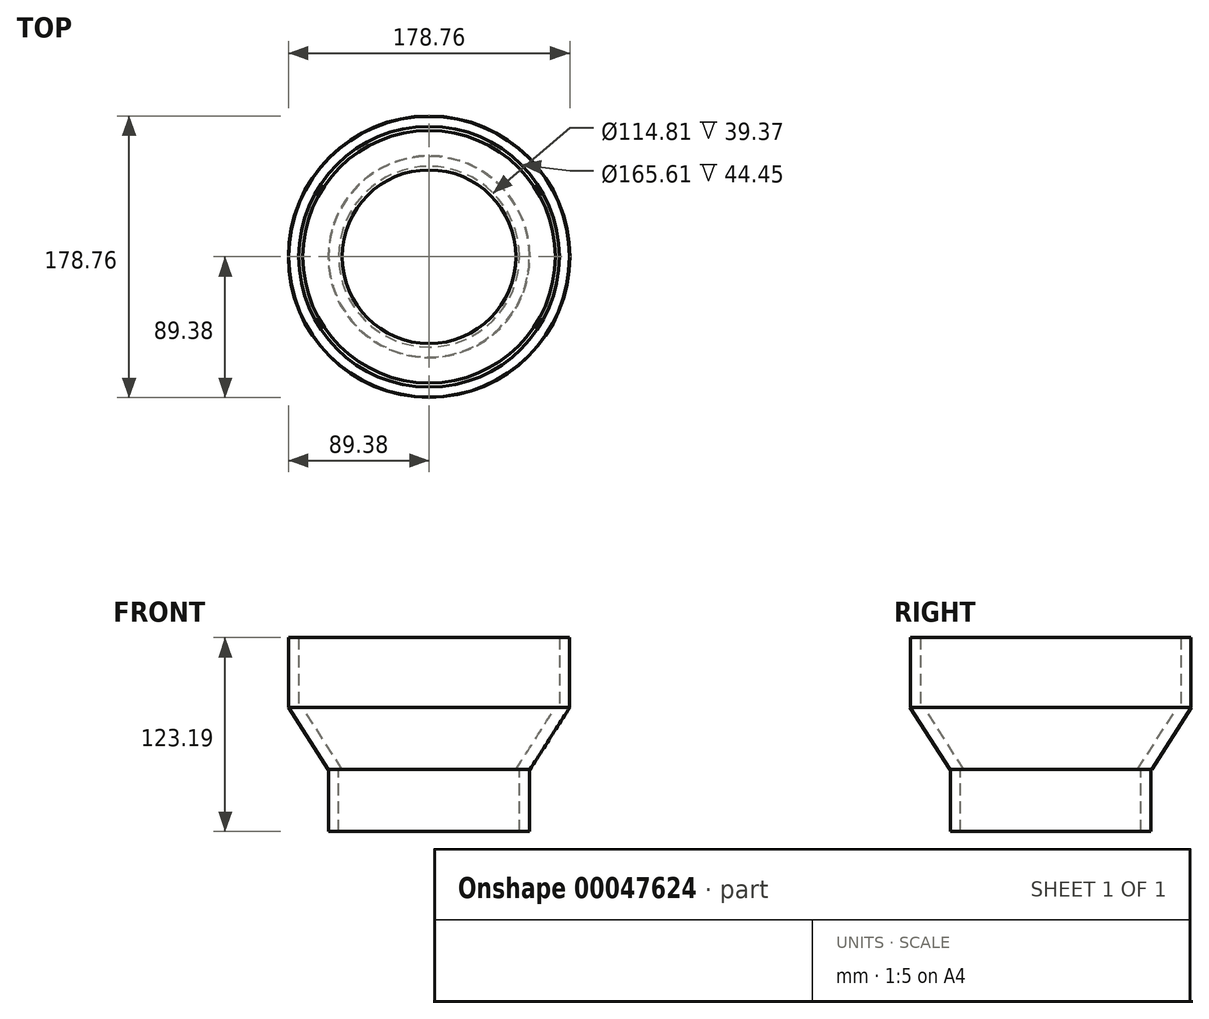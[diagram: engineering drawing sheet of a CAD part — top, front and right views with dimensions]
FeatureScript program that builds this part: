
annotation { "Feature Type Name" : "Feature", "Feature Type Description" : "" }
export const myFeature = defineFeature(function(context is Context, id is Id, definition is map)
    precondition{}
    {
        {
            var Q0;
            Q0=qCreatedBy(makeId("Top.planeOp"),FACE);
            var sketch = newSketch(context, id + "F0", { "sketchPlane" : qUnion([Q0])});
            skCircle(sketch, "E0", {"center": v(0, 0) * mm, "radius": 57.4 * mm});
            skSolve(sketch);
        }
        {
            var Q0;
            Q0=qCreatedBy(makeId("Top.planeOp"),FACE);
            var sketch = newSketch(context, id + "F1", { "sketchPlane" : qUnion([Q0])});
            skCircle(sketch, "E1", {"center": v(0, 0) * mm, "radius": 63.75 * mm});
            skSolve(sketch);
        }
        {
            var Q0;
            Q0=makeQuery(id+"F1.imprint","IMPRINT",FACE,{"disambiguationData":[TD([[makeQuery(id+"F1.imprint","IMPRINT",EDGE,{"derivedFrom":sQuery(id+"F1.wireOp",EDGE,"E1")}),1.0]])]});
            extrude(context, id + "F2", {"entities" : qUnion([Q0]), "oppositeDirection" : true, "depth" : 39.37 * mm});
        }
        {
            var Q0;
            Q0=makeQuery(id+"F0.imprint","IMPRINT",FACE,{"disambiguationData":[TD([[makeQuery(id+"F0.imprint","IMPRINT",EDGE,{"derivedFrom":sQuery(id+"F0.wireOp",EDGE,"E0")}),1.0]])]});
            extrude(context, id + "F3", {"entities" : qUnion([Q0]), "operationType" : NewBodyOperationType.REMOVE, "oppositeDirection" : true, "depth" : 39.37 * mm});
        }
        {
            var Q0;
            Q0=qCreatedBy(makeId("Top.planeOp"),FACE);
            cPlane(context, id + "F4", {"entities" : qUnion([Q0]), "cplaneType" : CPlaneType.OFFSET, "offset" : 39.37 * mm, "width" : 152.4 * mm, "height" : 152.4 * mm});
        }
        {
            var Q0;
            Q0=qCreatedBy(id+"F4.planeOp",FACE);
            var sketch = newSketch(context, id + "F5", { "sketchPlane" : qUnion([Q0])});
            skCircle(sketch, "E2", {"center": v(0, 0) * mm, "radius": 82.8 * mm});
            skCircle(sketch, "E3", {"center": v(0, 0) * mm, "radius": 89.15 * mm});
            skSolve(sketch);
        }
        {
            var Q0;
            Q0=makeQuery(id+"F5.imprint","IMPRINT",FACE,{"disambiguationData":[TD([[makeQuery(id+"F5.imprint","IMPRINT",EDGE,{"derivedFrom":sQuery(id+"F5.wireOp",EDGE,"E2")}),-1.0]])]});
            extrude(context, id + "F6", {"entities" : qUnion([Q0]), "depth" : 44.45 * mm});
        }
        {
            var Q0;
            Q0=qCreatedBy(makeId("Right.planeOp"),FACE);
            var sketch = newSketch(context, id + "F7", { "sketchPlane" : qUnion([Q0])});
            skLineSegment(sketch, "E4", {"start": v(-89.38, 39.5) * mm, "end": v(-64.1, 0) * mm});
            skLineSegment(sketch, "E5", {"start": v(-80.2, 39.27) * mm, "end": v(-55.15, 0) * mm});
            skLineSegment(sketch, "E6", {"start": v(-89.38, 39.5) * mm, "end": v(-80.2, 39.27) * mm});
            skLineSegment(sketch, "E7", {"start": v(-64.1, 0) * mm, "end": v(-55.15, 0) * mm});
            skLineSegment(sketch, "E8", {"start": v(0, 38.82) * mm, "end": v(0, 0) * mm});
            skSolve(sketch);
        }
        {
            var Q0;
            Q0=makeQuery(id+"F7.imprint","IMPRINT",FACE,{"disambiguationData":[TD([[makeQuery(id+"F7.imprint","IMPRINT",EDGE,{"derivedFrom":sQuery(id+"F7.wireOp",EDGE,"E4")}),1.0]])]});
            var Q1;
            Q1=sQuery(id+"F7.wireOp",EDGE,"E8");
            revolve(context, id + "F8", {"entities" : qUnion([Q0]), "axis" : qUnion([Q1]), "revolveType" : RevolveType.FULL});
        }
    });
